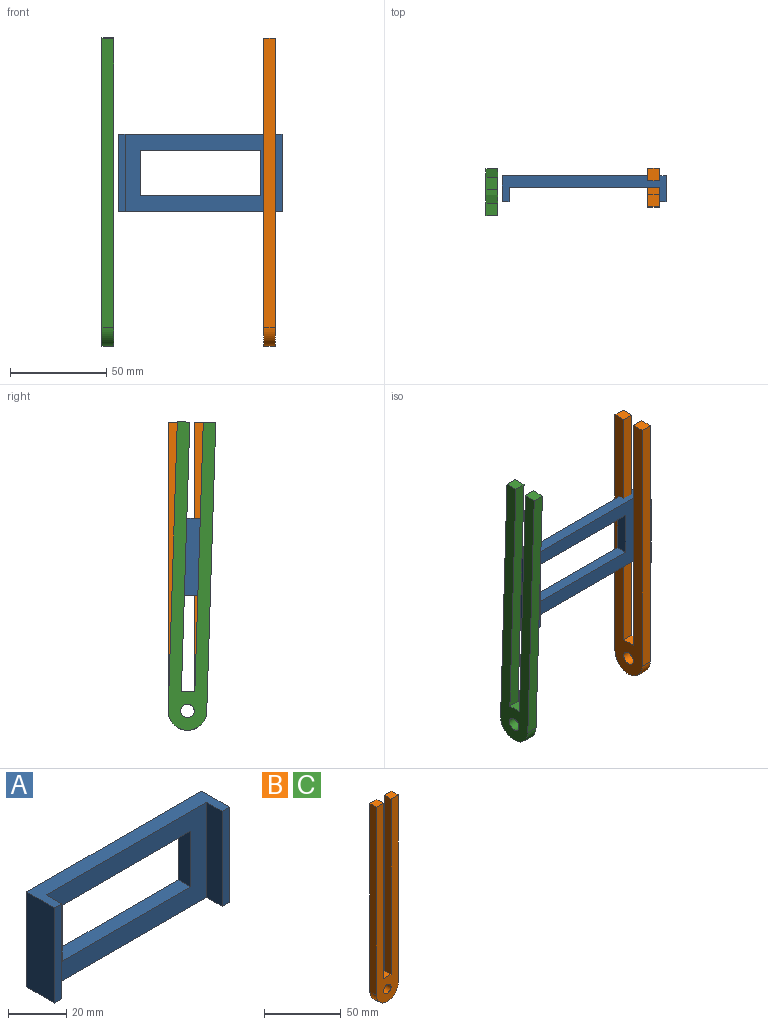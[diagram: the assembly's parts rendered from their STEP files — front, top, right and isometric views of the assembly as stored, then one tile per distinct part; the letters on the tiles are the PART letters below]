
ASSEMBLY  parts=3 mates=2
PART A: 14 faces, bbox 85x13.5x40 mm
  f0: plane 78x40mm, normal (0,-1,0), area 1651.2mm2, adj f2,f4,f6,f7,f8,f9,f10,f12
  f1: plane 85x40mm, normal (0,1,0), area 1931.2mm2, adj f2,f3,f4,f5,f6,f7,f8,f9
  f2: plane 85x13.5mm, normal (0,0,1), area 562.5mm2, adj f0,f1,f3,f5,f10,f11,f12,f13
  f3: plane 40x13.5mm, normal (-1,0,0), area 540mm2, adj f1,f2,f4,f13
  f4: plane 85x13.5mm, normal (0,0,-1), area 562.5mm2, adj f0,f1,f3,f5,f10,f11,f12,f13
  f5: plane 40x13.5mm, normal (1,0,0), area 540mm2, adj f1,f2,f4,f11
  f6: plane 62.5x6mm, normal (0,0,-1), area 375mm2, adj f0,f1,f7,f9
  f7: plane 23.5x6mm, normal (1,0,0), area 141mm2, adj f0,f1,f6,f8
  f8: plane 62.5x6mm, normal (0,0,1), area 375mm2, adj f0,f1,f7,f9
  f9: plane 23.5x6mm, normal (-1,0,0), area 141mm2, adj f0,f1,f6,f8
  f10: plane 40x7.5mm, normal (-1,0,0), area 300mm2, adj f0,f2,f4,f11
  f11: plane 40x3.5mm, normal (0,-1,0), area 140mm2, adj f2,f4,f5,f10
  f12: plane 40x7.5mm, normal (1,0,0), area 300mm2, adj f0,f2,f4,f13
  f13: plane 40x3.5mm, normal (0,-1,0), area 140mm2, adj f2,f3,f4,f12
PART B: 11 faces, bbox 20x6x160 mm
  f0: plane 6.5x6mm, normal (0,0,1), area 39mm2, adj f1,f2,f3,f9
  f1: plane 160x20mm, normal (0,1,0), area 2138.6mm2, adj f0,f3,f4,f5,f6,f7,f8,f9
  f2: plane 160x20mm, normal (0,-1,0), area 2138.6mm2, adj f0,f3,f4,f5,f6,f7,f8,f9
  f3: plane 150x6mm, normal (1,0,0), area 900mm2, adj f0,f1,f2,f7
  f4: plane 6.5x6mm, normal (0,0,1), area 39mm2, adj f1,f2,f5,f10
  f5: plane 150x6mm, normal (-1,0,0), area 900mm2, adj f1,f2,f4,f7
  f6: cylinder r=3.5mm len=7mm, axis (0,-1,0), area 131.9mm2, adj f1,f2
  f7: cylinder r=10mm len=20mm, axis (0,-1,0), area 188.5mm2, adj f1,f2,f3,f5
  f8: plane 7x6mm, normal (0,0,1), area 42mm2, adj f1,f2,f9,f10
  f9: plane 140x6mm, normal (-1,0,0), area 840mm2, adj f0,f1,f2,f8
  f10: plane 140x6mm, normal (1,0,0), area 840mm2, adj f1,f2,f4,f8
PART C: same geometry as B
PLACE A rot(axis=(-0.29,0,-0.96),0deg) t=(-22.96,63.74,33.47)mm
PLACE B rot(axis=(0,0,1),90deg) t=(16.04,57.49,-46.53)mm fixed
PLACE C rot(axis=(0.02,-0.02,1),90deg) t=(-67.96,57.49,-46.53)mm
MATE fastened A.f10 <-> B.f2  axis (-1,0,0) through (16.04,53.99,33.47)mm
MATE revolute C.f6 <-> B.f6  axis (1,0,0) through (-67.96,57.49,-46.53)mm
